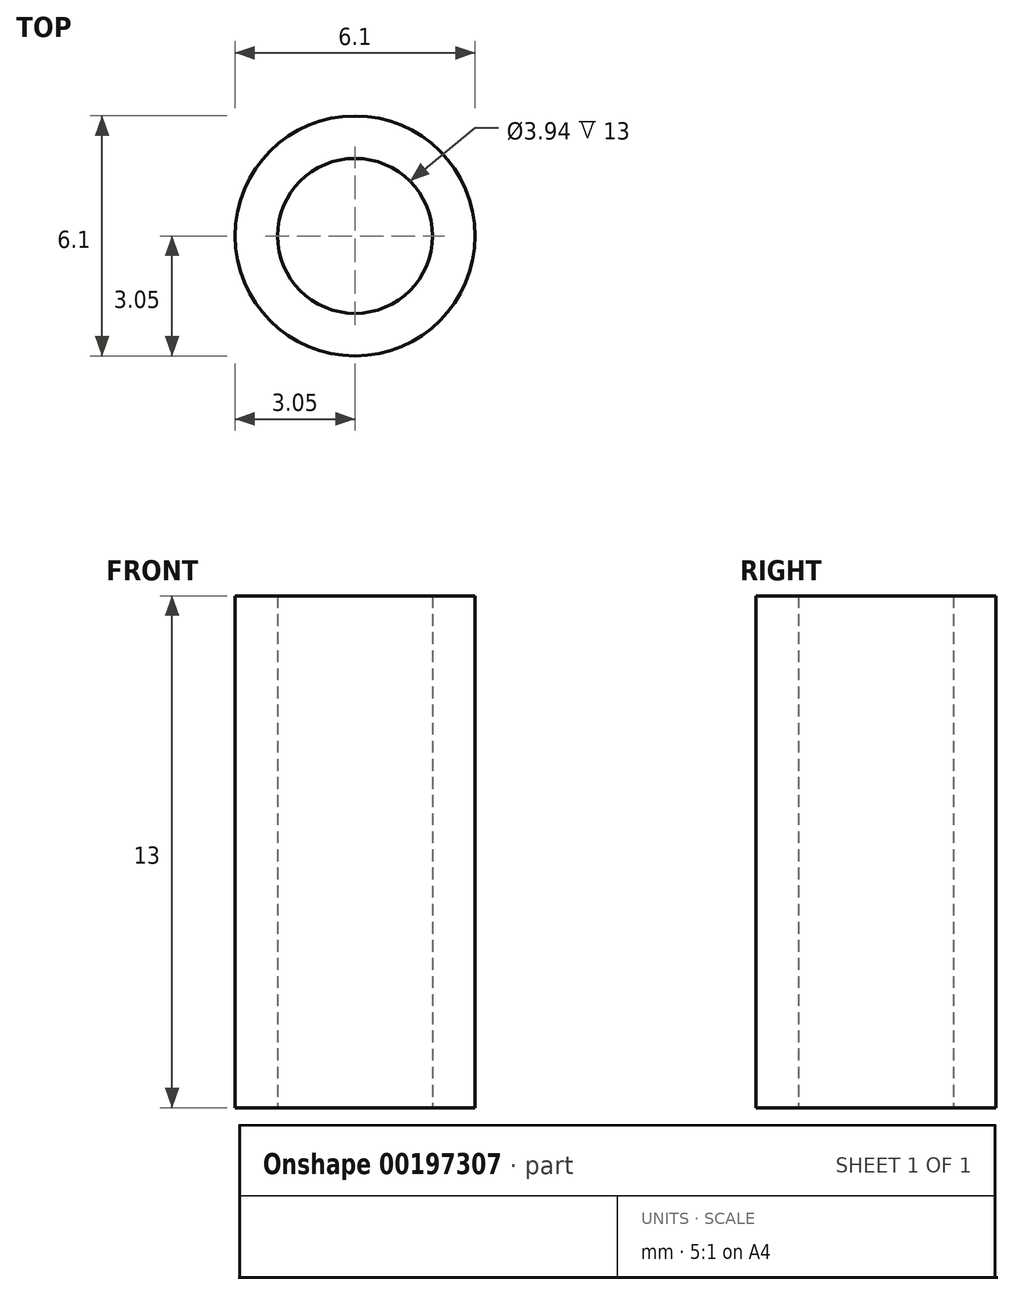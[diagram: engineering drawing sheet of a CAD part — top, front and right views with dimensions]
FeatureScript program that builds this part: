
annotation { "Feature Type Name" : "Feature", "Feature Type Description" : "" }
export const myFeature = defineFeature(function(context is Context, id is Id, definition is map)
    precondition{}
    {
        {
            var Q0;
            Q0=qCreatedBy(makeId("Top.planeOp"),FACE);
            var sketch = newSketch(context, id + "F0", { "sketchPlane" : qUnion([Q0])});
            skCircle(sketch, "E0", {"center": v(0, 0) * mm, "radius": 1.97 * mm});
            skCircle(sketch, "E1", {"center": v(0, 0) * mm, "radius": 3.05 * mm});
            skSolve(sketch);
        }
        {
            var Q0;
            Q0=makeQuery(id+"F0.imprint","IMPRINT",FACE,{"disambiguationData":[TD([[makeQuery(id+"F0.imprint","IMPRINT",EDGE,{"derivedFrom":sQuery(id+"F0.wireOp",EDGE,"E0")}),-1.0]])]});
            extrude(context, id + "F1", {"entities" : qUnion([Q0]), "depth" : 13 * mm});
        }
    });
